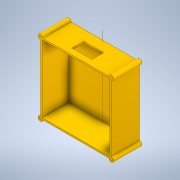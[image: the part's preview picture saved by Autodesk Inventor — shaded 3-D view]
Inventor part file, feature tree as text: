
AUTODESK INVENTOR PART (.ipt)
format: ipt  version: 2022 (Build 260153000, 153)  size: 175,616 bytes
history: native  units: in
note: dims shown in document units (in); Inventor stores cm internally (conversion verified against a paired STEP export)
features: extrude x4, sketch x4, shell x1
ambient origin geometry x8: Origin, YZ Plane, XZ Plane, XY Plane, X Axis, Y Axis, Z Axis, Center Point
bodies: Solid1 (feature_tree)
feature tree (9):
  extrude  "Extrusion1"  Depth=2.0in TaperAngle=0.0deg
  shell  "Shell1"  Thickness=0.125in
  extrude  "Extrusion2"  Depth=2.0in TaperAngle=0.0deg
  extrude  "Extrusion3"  Depth=1.5in
  extrude  "Extrusion4"  Depth=0.45in
  sketch  "Sketch1"  dims[d0=5.1in d1=2.0in d2=0.0in d3=0.125in]
  sketch  "Sketch2"  dims[d4=0.376in d5=2.0in d6=0.125in d7=0.0in d8=0.0in]
  sketch  "Sketch3"  dims[d10=4.25in d11=0.0in d12=1.5in]
  sketch  "Sketch4"  dims[d13=0.89in d14=0.45in d15=1.0in d16=0.0in d17=0.1417in]
